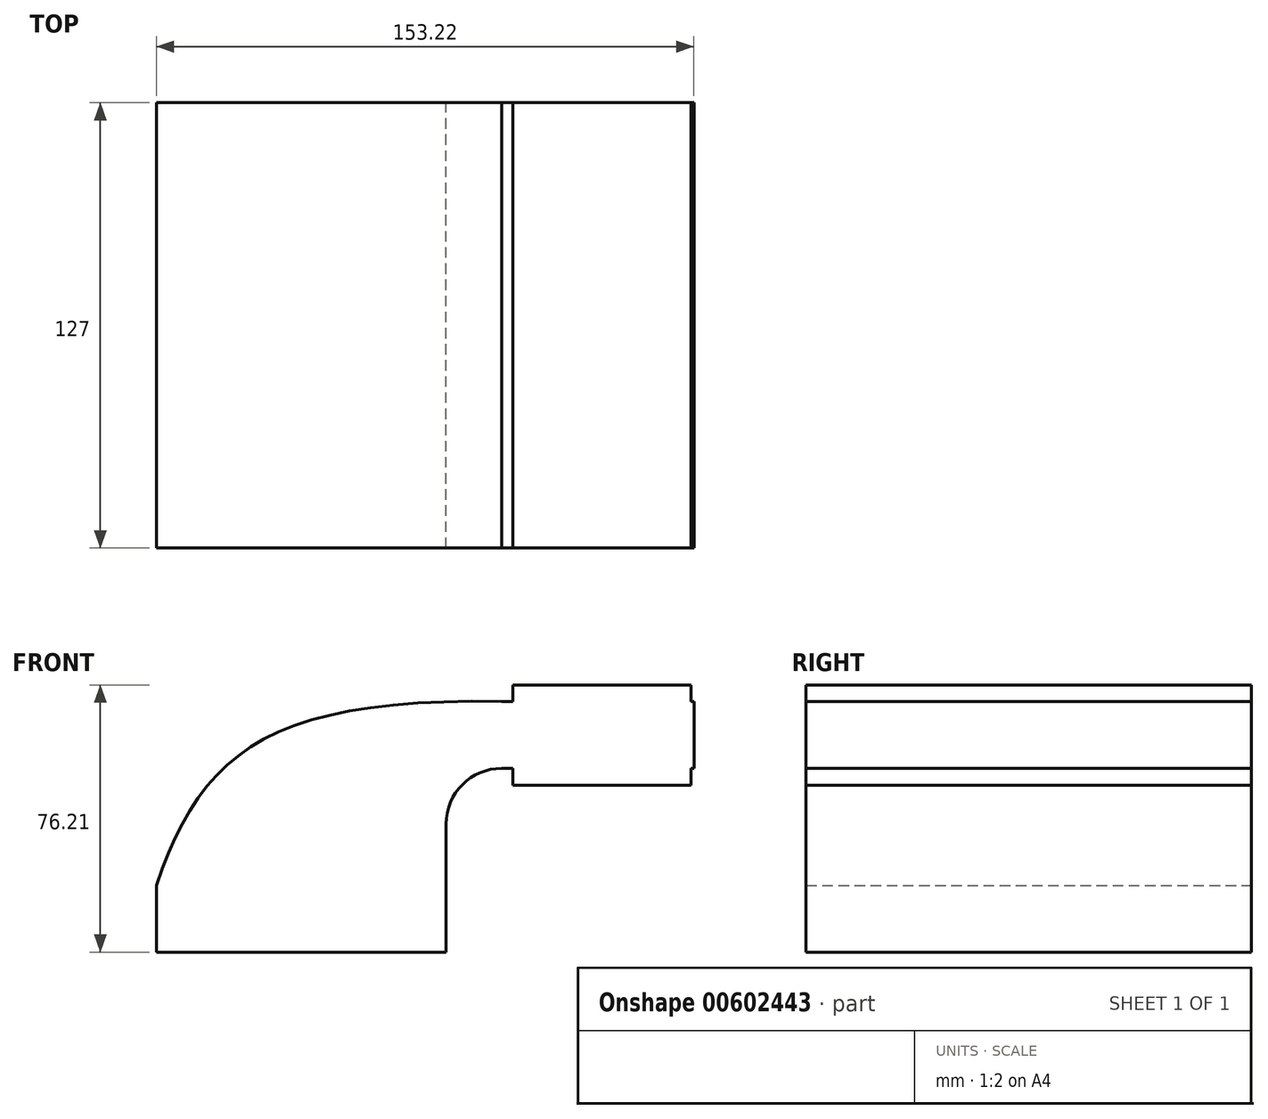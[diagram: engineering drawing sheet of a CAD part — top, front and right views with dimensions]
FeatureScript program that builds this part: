
annotation { "Feature Type Name" : "Feature", "Feature Type Description" : "" }
export const myFeature = defineFeature(function(context is Context, id is Id, definition is map)
    precondition{}
    {
        {
            var Q0;
            Q0=qCreatedBy(makeId("Front.planeOp"),FACE);
            var sketch = newSketch(context, id + "F0", { "sketchPlane" : qUnion([Q0])});
            skLineSegment(sketch, "E0.bottom", {"start": v(-41.28, -9.53) * mm, "end": v(41.28, -9.53) * mm});
            skLineSegment(sketch, "E0.top", {"start": v(-41.28, 9.52) * mm, "end": v(41.28, 9.52) * mm});
            skLineSegment(sketch, "E0.left", {"start": v(-41.28, -9.53) * mm, "end": v(-41.28, 9.52) * mm});
            skLineSegment(sketch, "E0.right", {"start": v(41.28, -9.53) * mm, "end": v(41.28, 9.52) * mm});
            skPoint(sketch, "E0.middle", {"position": v(0, 0) * mm});
            skLineSegment(sketch, "E1.bottom", {"start": v(60.32, 38.1) * mm, "end": v(111.12, 38.1) * mm});
            skLineSegment(sketch, "E1.top", {"start": v(60.32, 66.67) * mm, "end": v(111.12, 66.67) * mm});
            skLineSegment(sketch, "E1.left", {"start": v(60.32, 38.1) * mm, "end": v(60.32, 66.67) * mm});
            skLineSegment(sketch, "E1.right", {"start": v(111.12, 38.1) * mm, "end": v(111.12, 66.67) * mm});
            skPoint(sketch, "E1.middle", {"position": v(85.72, 52.39) * mm});
            skLineSegment(sketch, "E2", {"start": v(41.27, 9.52) * mm, "end": v(41.27, 27) * mm});
            skArc(sketch, "E3", {"start": v(41.27, 27) * mm, "mid": v(45.92, 38.23) * mm, "end": v(57.15, 42.88) * mm});
            skLineSegment(sketch, "E4", {"start": v(57.15, 42.88) * mm, "end": v(111.94, 42.88) * mm});
            skLineSegment(sketch, "E5.0", {"start": v(57.15, 61.93) * mm, "end": v(111.94, 61.93) * mm});
            skArc(sketch, "E5.1", {"start": v(22.23, 27) * mm, "mid": v(32.45, 51.7) * mm, "end": v(57.15, 61.93) * mm});
            skLineSegment(sketch, "E5.2", {"start": v(22.23, 21.68) * mm, "end": v(22.23, 27) * mm});
            skLineSegment(sketch, "E6", {"start": v(111.94, 61.93) * mm, "end": v(111.94, 42.88) * mm});
            skFitSpline(sketch, "E7", {"points": [v(-41.28, 9.53) * mm, v(57.15, 61.93) * mm], "startDerivative": vector(37.56, 111.32) * mm, "endDerivative": vector(201.58, -3.75) * mm});
            skSolve(sketch);
        }
        {
            var Q0;
            {var subQ0=sQuery(id+"F0.wireOp",EDGE,"E1.bottom");Q0=makeQuery(id+"F0.imprint","IMPRINT",FACE,{"disambiguationData":[TD([[makeQuery(id+"F0.imprint","IMPRINT",EDGE,{"derivedFrom":subQ0}),1.0]])]});}
            var Q1;
            {var subQ0=sQuery(id+"F0.wireOp",EDGE,"E1.top");Q1=makeQuery(id+"F0.imprint","IMPRINT",FACE,{"disambiguationData":[TD([[makeQuery(id+"F0.imprint","IMPRINT",EDGE,{"derivedFrom":subQ0}),-1.0]])]});}
            var Q2;
            {var subQ5=sQuery(id+"F0.wireOp",EDGE,"E6");Q2=makeQuery(id+"F0.imprint","IMPRINT",FACE,{"disambiguationData":[TD([[makeQuery(id+"F0.imprint","IMPRINT",EDGE,{"derivedFrom":subQ5}),-1.0]])]});}
            var Q3;
            Q3=makeQuery(id+"F0.imprint","IMPRINT",FACE,{"disambiguationData":[TD([[makeQuery(id+"F0.imprint","IMPRINT",EDGE,{"derivedFrom":sQuery(id+"F0.wireOp",EDGE,"E0.top")}),1.0]])]});
            var Q4;
            {var subQ0=sQuery(id+"F0.wireOp",EDGE,"E4");var subQ1=sQuery(id+"F0.wireOp",EDGE,"E1.left");var subQ2=makeQuery(id+"F0.imprint","INTERSECT",VERTEX,{"derivedFrom":[subQ1,subQ0]});Q4=makeQuery(id+"F0.imprint","IMPRINT",FACE,{"disambiguationData":[TD([[makeQuery(id+"F0.imprint","IMPRINT",EDGE,{"disambiguationData":[TD([[subQ2,-1.0]])],"derivedFrom":subQ1}),-1.0]])]});}
            var Q5;
            Q5=makeQuery(id+"F0.imprint","IMPRINT",FACE,{"disambiguationData":[TD([[makeQuery(id+"F0.imprint","IMPRINT",EDGE,{"derivedFrom":sQuery(id+"F0.wireOp",EDGE,"E0.bottom")}),1.0]])]});
            extrude(context, id + "F1", {"entities" : qUnion([Q0, Q1, Q2, Q3, Q4, Q5]), "depth" : 127 * mm, "offsetDistance" : 25.4 * mm});
        }
    });
